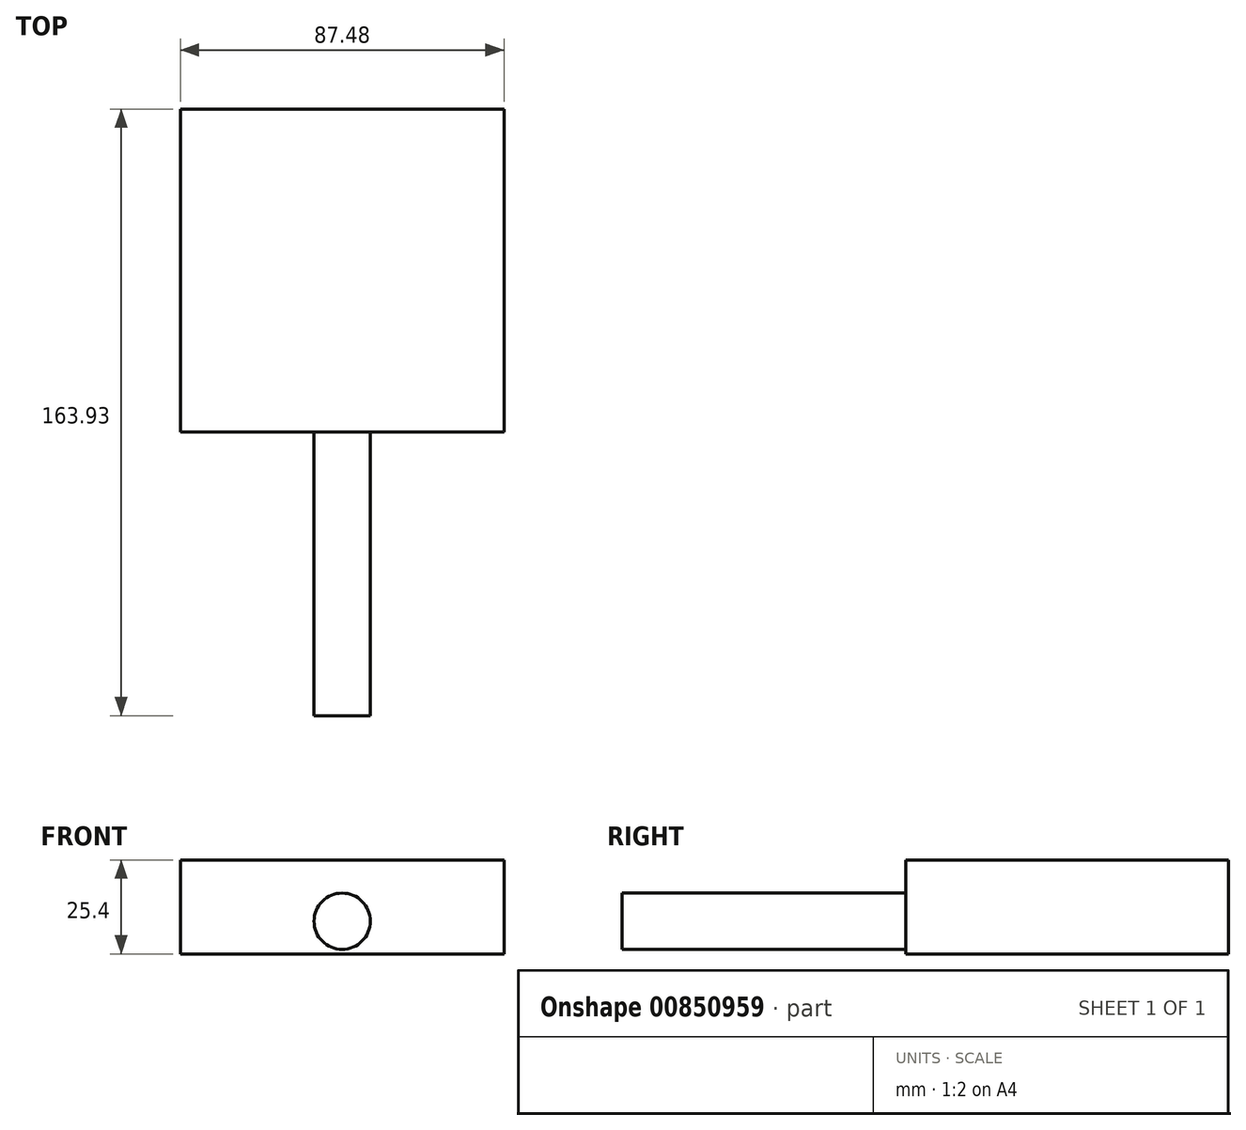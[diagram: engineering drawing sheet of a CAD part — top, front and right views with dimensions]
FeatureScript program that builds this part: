
annotation { "Feature Type Name" : "Feature", "Feature Type Description" : "" }
export const myFeature = defineFeature(function(context is Context, id is Id, definition is map)
    precondition{}
    {
        {
            var Q0;
            Q0=qCreatedBy(makeId("Top.planeOp"),FACE);
            var sketch = newSketch(context, id + "F0", { "sketchPlane" : qUnion([Q0])});
            skLineSegment(sketch, "E0.bottom", {"start": v(-35.36, 50.06) * mm, "end": v(52.12, 50.06) * mm});
            skLineSegment(sketch, "E0.top", {"start": v(-35.36, -37.16) * mm, "end": v(52.12, -37.16) * mm});
            skLineSegment(sketch, "E0.left", {"start": v(-35.36, 50.06) * mm, "end": v(-35.36, -37.16) * mm});
            skLineSegment(sketch, "E0.right", {"start": v(52.12, 50.06) * mm, "end": v(52.12, -37.16) * mm});
            skSolve(sketch);
        }
        {
            var Q0;
            Q0=makeQuery(id+"F0.imprint","IMPRINT",FACE,{"disambiguationData":[TD([[makeQuery(id+"F0.imprint","IMPRINT",EDGE,{"derivedFrom":sQuery(id+"F0.wireOp",EDGE,"E0.bottom")}),-1.0]])]});
            extrude(context, id + "F1", {"entities" : qUnion([Q0]), "depth" : 25.4 * mm, "offsetDistance" : 25.4 * mm});
        }
        {
            var Q0;
            Q0=makeQuery(id+"F1.opExtrude","SWEPT_FACE",FACE,{"disambiguationData":[OSD([sQuery(id+"F0.wireOp",EDGE,"E0.top")])]});
            var sketch = newSketch(context, id + "F2", { "sketchPlane" : qUnion([Q0])});
            skCircle(sketch, "E1", {"center": v(8.38, 8.83) * mm, "radius": 7.6 * mm});
            skPoint(sketch, "E1.centerSnap0", {"position": v(8.38, 25.4) * mm});
            skSolve(sketch);
        }
        {
            var Q0;
            Q0=makeQuery(id+"F2.imprint","IMPRINT",FACE,{"disambiguationData":[TD([[makeQuery(id+"F2.imprint","IMPRINT",EDGE,{"derivedFrom":sQuery(id+"F2.wireOp",EDGE,"E1")}),1.0]])]});
            extrude(context, id + "F3", {"entities" : qUnion([Q0]), "depth" : 76.7 * mm, "offsetDistance" : 25.4 * mm});
        }
    });
